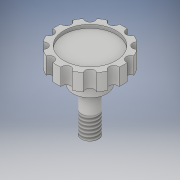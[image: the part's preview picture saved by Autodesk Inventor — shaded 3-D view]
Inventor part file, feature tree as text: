
AUTODESK INVENTOR PART (.ipt)
format: ipt  version: 2018 (Build 220112000, 112)  size: 161,792 bytes
history: native  units: in
note: dims shown in document units (in); Inventor stores cm internally (conversion verified against a paired STEP export)
features: sketch x3, hole x2, revolve x1, pattern_circular x1, thread x1
ambient origin geometry x8: Origin, YZ Plane, XZ Plane, XY Plane, X Axis, Y Axis, Z Axis, Center Point
bodies: Solid1 (feature_tree)
feature tree (8):
  revolve  "Revolution1"  [1 undecoded]
  sketch  "Sketch2"  dims[d2=0.25in d3=0.25in]
  hole  "Hole1"  [1 undecoded]
  pattern_circular  "Circular Pattern1"  [2 undecoded]
  hole  "Hole2"  [1 undecoded]
  thread  "Thread1"  [1 undecoded]
  sketch  "Sketch1"  dims[d0=1.15in d1=0.5in]
  sketch  "Sketch3"  dims[d4=0.25in d5=0.125in d6=90.0deg d7=0.78in d8=0.5in d9=15.0deg d10=0.14in d11=0.75in d12=0.375in d13=0.25in d14=0.5635in d15=1.0in d16=0.8108in d17=4.7244in d18=360.0deg d20=0.78in d21=0.75in d22=0.375in d23=0.25in d24=0.5635in d25=0.05in d26=0.0in d27=1.0in d28=0.32in]
note: 6 required parameter values undecoded (feature->parameter linkage not recoverable at this tier; creation-order binding heuristic only, values carry confidence <= 0.55)